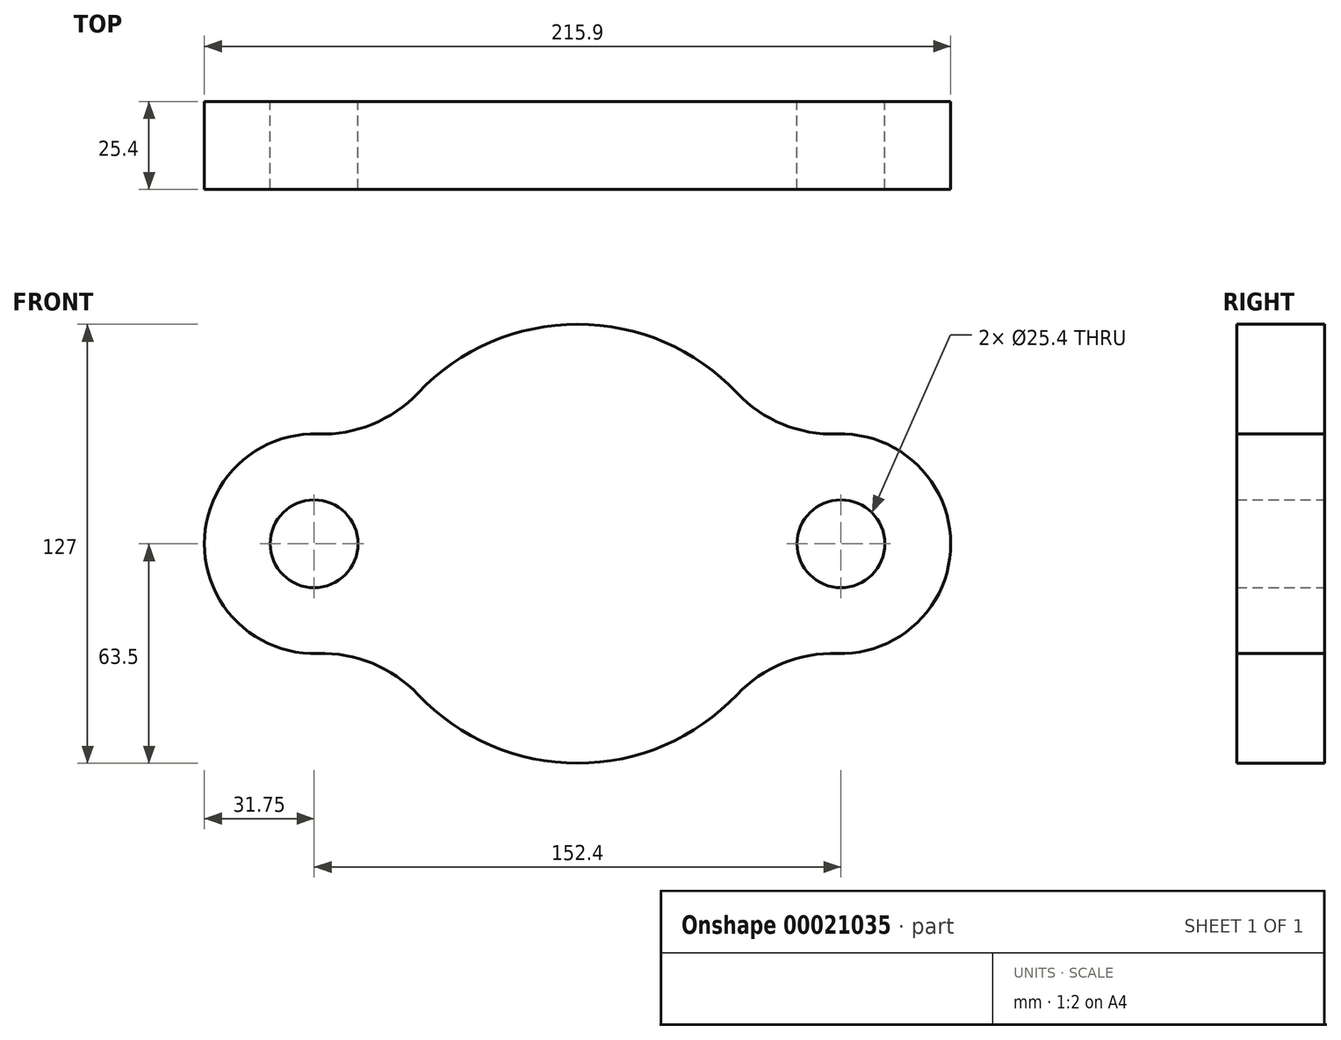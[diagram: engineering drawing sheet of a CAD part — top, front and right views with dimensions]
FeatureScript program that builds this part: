
annotation { "Feature Type Name" : "Feature", "Feature Type Description" : "" }
export const myFeature = defineFeature(function(context is Context, id is Id, definition is map)
    precondition{}
    {
        {
            var Q0;
            Q0=qCreatedBy(makeId("Front.planeOp"),FACE);
            var sketch = newSketch(context, id + "F0", { "sketchPlane" : qUnion([Q0])});
            skArc(sketch, "E0", {"start": v(46.14, 43.63) * mm, "mid": v(0, 63.5) * mm, "end": v(-46.14, 43.63) * mm});
            skCircle(sketch, "E1", {"center": v(0, 0) * mm, "radius": 44.45 * mm});
            skCircle(sketch, "E2", {"center": v(-76.2, 0) * mm, "radius": 12.7 * mm});
            skCircle(sketch, "E3", {"center": v(76.2, 0) * mm, "radius": 12.7 * mm});
            skArc(sketch, "E4", {"start": v(-75.12, 31.73) * mm, "mid": v(-107.95, 0) * mm, "end": v(-75.12, -31.73) * mm});
            skArc(sketch, "E5", {"start": v(75.12, -31.73) * mm, "mid": v(107.95, 0) * mm, "end": v(75.12, 31.73) * mm});
            skArc(sketch, "E6", {"start": v(-46.14, -43.63) * mm, "mid": v(-59.35, -34.56) * mm, "end": v(-75.12, -31.73) * mm});
            skArc(sketch, "E7", {"start": v(-75.12, 31.73) * mm, "mid": v(-59.35, 34.56) * mm, "end": v(-46.14, 43.63) * mm});
            skArc(sketch, "E8", {"start": v(46.14, 43.63) * mm, "mid": v(59.35, 34.56) * mm, "end": v(75.12, 31.73) * mm});
            skArc(sketch, "E9", {"start": v(75.12, -31.73) * mm, "mid": v(59.35, -34.56) * mm, "end": v(46.14, -43.63) * mm});
            skPoint(sketch, "E10.orphan", {"position": v(-36.3, -76.39) * mm});
            skPoint(sketch, "E11.orphan", {"position": v(91.73, -36.18) * mm});
            skPoint(sketch, "E12.orphan", {"position": v(-37.48, 81.25) * mm});
            skPoint(sketch, "E13.orphan", {"position": v(110.32, 80.72) * mm});
            skArc(sketch, "E14.trimOffspring", {"start": v(-46.14, -43.63) * mm, "mid": v(0, -63.5) * mm, "end": v(46.14, -43.63) * mm});
            skSolve(sketch);
        }
        {
            var Q0;
            Q0 = qSketchRegion(id + "F0", true);
            var Q1;
            Q1=makeQuery(id+"F0.imprint","IMPRINT",FACE,{"disambiguationData":[TD([[makeQuery(id+"F0.imprint","IMPRINT",EDGE,{"derivedFrom":sQuery(id+"F0.wireOp",EDGE,"E1")}),1.0]])]});
            extrude(context, id + "F1", {"entities" : qUnion([Q0, Q1]), "depth" : 25.4 * mm});
        }
    });
